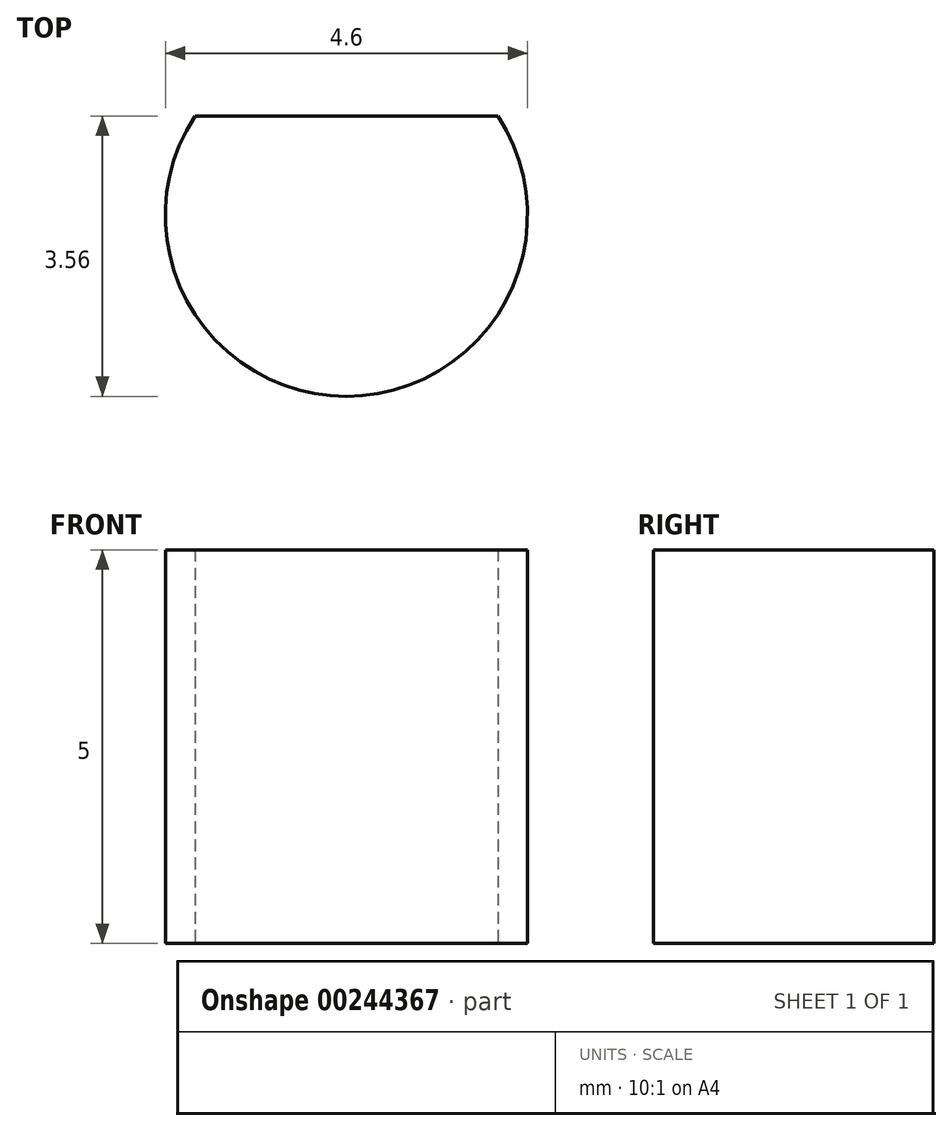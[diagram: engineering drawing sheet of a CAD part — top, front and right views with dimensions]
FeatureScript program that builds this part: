
annotation { "Feature Type Name" : "Feature", "Feature Type Description" : "" }
export const myFeature = defineFeature(function(context is Context, id is Id, definition is map)
    precondition{}
    {
        {
            var Q0;
            Q0=qCreatedBy(makeId("Top.planeOp"),FACE);
            var sketch = newSketch(context, id + "F0", { "sketchPlane" : qUnion([Q0])});
            skArc(sketch, "E0", {"start": v(-1.92, 1.26) * mm, "mid": v(0, -2.3) * mm, "end": v(1.92, 1.26) * mm});
            skLineSegment(sketch, "E1", {"start": v(-2.55, 1.26) * mm, "end": v(3.2, 1.26) * mm});
            skSolve(sketch);
        }
        {
            var Q0;
            Q0 = qSketchRegion(id + "F0", true);
            extrude(context, id + "F1", {"entities" : qUnion([Q0]), "depth" : 5 * mm});
        }
    });
